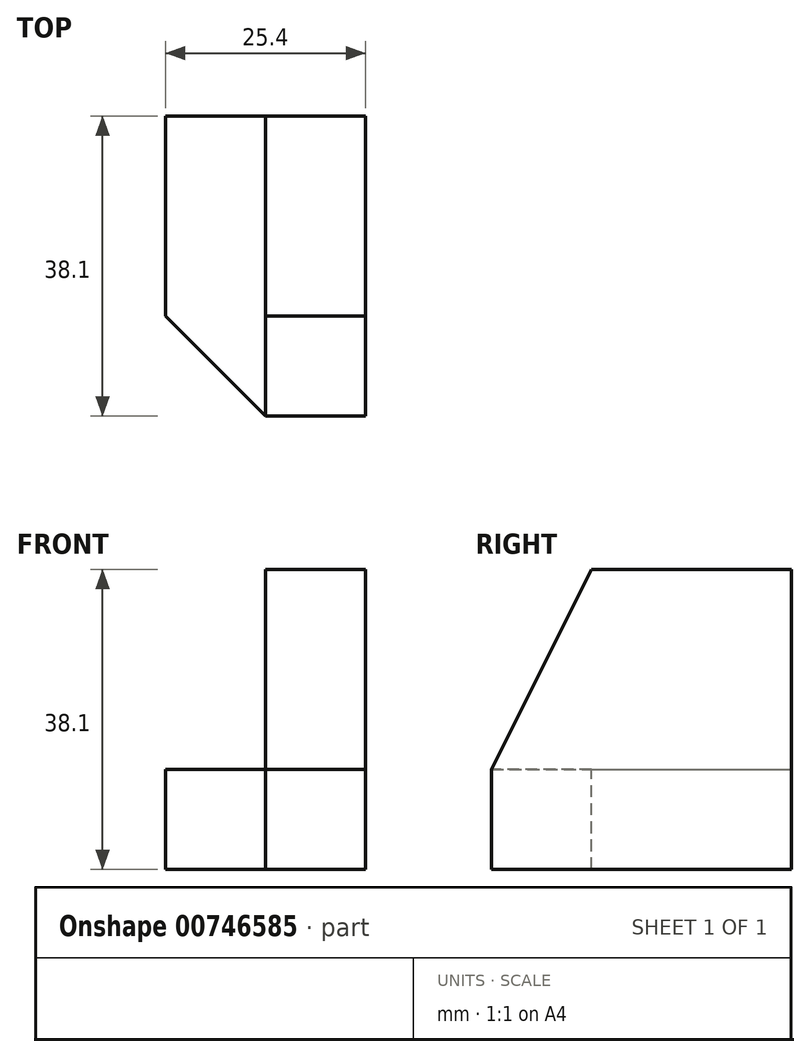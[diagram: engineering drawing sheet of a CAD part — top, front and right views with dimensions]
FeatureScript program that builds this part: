
annotation { "Feature Type Name" : "Feature", "Feature Type Description" : "" }
export const myFeature = defineFeature(function(context is Context, id is Id, definition is map)
    precondition{}
    {
        {
            var Q0;
            Q0=qCreatedBy(makeId("Front.planeOp"),FACE);
            var sketch = newSketch(context, id + "F0", { "sketchPlane" : qUnion([Q0])});
            skLineSegment(sketch, "E0", {"start": v(0, 0) * mm, "end": v(25.4, 0) * mm});
            skLineSegment(sketch, "E1", {"start": v(25.4, 0) * mm, "end": v(25.4, 38.1) * mm});
            skLineSegment(sketch, "E2", {"start": v(25.4, 38.1) * mm, "end": v(12.7, 38.1) * mm});
            skLineSegment(sketch, "E3", {"start": v(12.7, 38.1) * mm, "end": v(12.7, 12.7) * mm});
            skLineSegment(sketch, "E4", {"start": v(12.7, 12.7) * mm, "end": v(0, 12.7) * mm});
            skLineSegment(sketch, "E5", {"start": v(0, 12.7) * mm, "end": v(0, 0) * mm});
            skSolve(sketch);
        }
        {
            var Q0;
            Q0=makeQuery(id+"F0.imprint","IMPRINT",FACE,{"disambiguationData":[TD([[makeQuery(id+"F0.imprint","IMPRINT",EDGE,{"derivedFrom":sQuery(id+"F0.wireOp",EDGE,"E0")}),1.0]])]});
            extrude(context, id + "F1", {"entities" : qUnion([Q0]), "depth" : 38.1 * mm, "offsetDistance" : 25.4 * mm});
        }
        {
            var Q0;
            Q0=makeQuery(id+"F1.opExtrude","CAP_FACE",FACE,{"disambiguationData":[OSD([sQuery(id+"F0.wireOp",EDGE,"E0"),sQuery(id+"F0.wireOp",EDGE,"E1"),sQuery(id+"F0.wireOp",EDGE,"E2"),sQuery(id+"F0.wireOp",EDGE,"E3"),sQuery(id+"F0.wireOp",EDGE,"E4"),sQuery(id+"F0.wireOp",EDGE,"E5")])],"isStart":false});
            var sketch = newSketch(context, id + "F2", { "sketchPlane" : qUnion([Q0])});
            skLineSegment(sketch, "E6", {"start": v(0, 38.1) * mm, "end": v(12.7, 12.7) * mm});
            skLineSegment(sketch, "E7", {"start": v(12.7, 12.7) * mm, "end": v(25.4, 12.7) * mm});
            skLineSegment(sketch, "E8", {"start": v(0, 38.1) * mm, "end": v(25.4, 38.1) * mm});
            skLineSegment(sketch, "E9", {"start": v(25.4, 38.1) * mm, "end": v(25.4, 12.7) * mm});
            skSolve(sketch);
        }
        {
            var Q0;
            {var subQ0=sQuery(id+"F2.wireOp",EDGE,"E6");Q0=makeQuery(id+"F2.imprint","IMPRINT",FACE,{"disambiguationData":[TD([[makeQuery(id+"F2.imprint","IMPRINT",EDGE,{"derivedFrom":subQ0}),1.0]])]});}
            extrude(context, id + "F3", {"entities" : qUnion([Q0]), "operationType" : NewBodyOperationType.REMOVE, "oppositeDirection" : true, "depth" : 12.7 * mm, "offsetDistance" : 25.4 * mm});
        }
        {
            var Q0;
            Q0=makeQuery(id+"F1.opExtrude","SWEPT_FACE",FACE,{"disambiguationData":[OSD([sQuery(id+"F0.wireOp",EDGE,"E3")])]});
            var sketch = newSketch(context, id + "F4", { "sketchPlane" : qUnion([Q0])});
            skLineSegment(sketch, "E10", {"start": v(25.4, 38.1) * mm, "end": v(38.1, 12.7) * mm});
            skLineSegment(sketch, "E11", {"start": v(25.4, 38.1) * mm, "end": v(38.1, 38.1) * mm});
            skLineSegment(sketch, "E12", {"start": v(38.1, 38.1) * mm, "end": v(38.1, 28.94) * mm});
            skSolve(sketch);
        }
        {
            var Q0;
            {var subQ0=sQuery(id+"F4.wireOp",EDGE,"E10");Q0=makeQuery(id+"F4.imprint","IMPRINT",FACE,{"disambiguationData":[TD([[makeQuery(id+"F4.imprint","IMPRINT",EDGE,{"derivedFrom":subQ0}),1.0]])]});}
            extrude(context, id + "F5", {"entities" : qUnion([Q0]), "operationType" : NewBodyOperationType.REMOVE, "oppositeDirection" : true, "depth" : 12.7 * mm, "offsetDistance" : 25.4 * mm});
        }
        {
            var Q0;
            Q0=makeQuery(id+"F1.opExtrude","SWEPT_FACE",FACE,{"disambiguationData":[OSD([sQuery(id+"F0.wireOp",EDGE,"E4")])]});
            var sketch = newSketch(context, id + "F6", { "sketchPlane" : qUnion([Q0])});
            skLineSegment(sketch, "E13", {"start": v(0, -25.4) * mm, "end": v(12.7, -38.1) * mm});
            skLineSegment(sketch, "E14", {"start": v(12.7, -38.1) * mm, "end": v(0, -38.1) * mm});
            skLineSegment(sketch, "E15", {"start": v(0, -38.1) * mm, "end": v(0, -25.4) * mm});
            skSolve(sketch);
        }
        {
            var Q0;
            Q0=makeQuery(id+"F6.imprint","IMPRINT",FACE,{"disambiguationData":[TD([[makeQuery(id+"F6.imprint","IMPRINT",EDGE,{"derivedFrom":sQuery(id+"F6.wireOp",EDGE,"E13")}),-1.0]])]});
            extrude(context, id + "F7", {"entities" : qUnion([Q0]), "operationType" : NewBodyOperationType.REMOVE, "oppositeDirection" : true, "depth" : 12.7 * mm, "offsetDistance" : 25.4 * mm});
        }
    });
